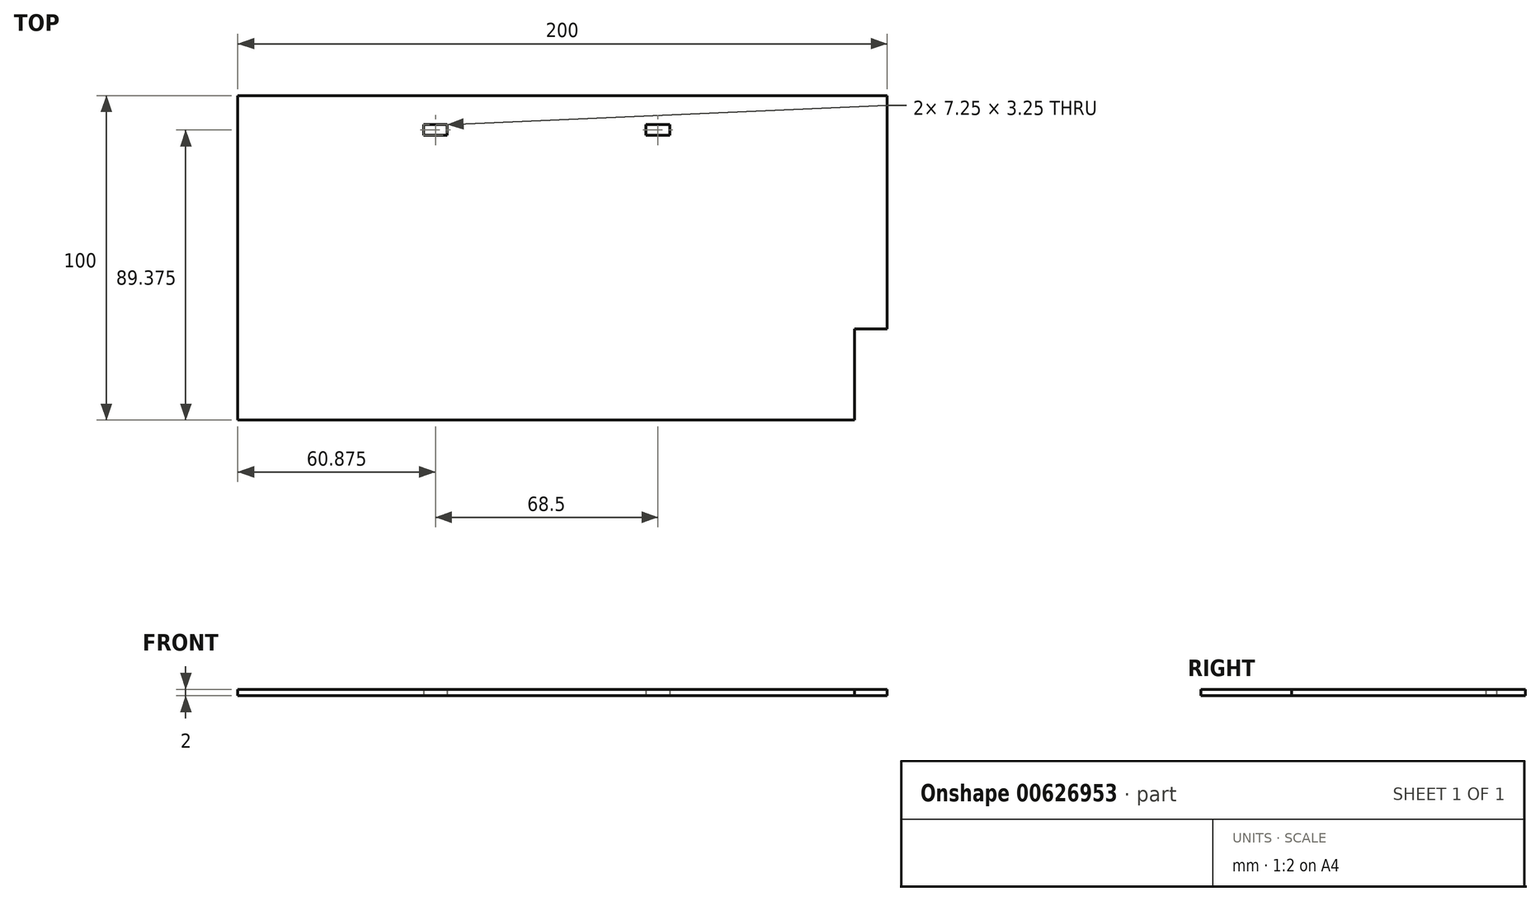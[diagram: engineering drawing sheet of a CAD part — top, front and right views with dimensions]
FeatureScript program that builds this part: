
annotation { "Feature Type Name" : "Feature", "Feature Type Description" : "" }
export const myFeature = defineFeature(function(context is Context, id is Id, definition is map)
    precondition{}
    {
        {
            var Q0;
            Q0=qCreatedBy(makeId("Top.planeOp"),FACE);
            var sketch = newSketch(context, id + "F0", { "sketchPlane" : qUnion([Q0])});
            skLineSegment(sketch, "E0.bottom", {"start": v(100, 50) * mm, "end": v(-100, 50) * mm});
            skLineSegment(sketch, "E0.top", {"start": v(90, -50) * mm, "end": v(-100, -50) * mm});
            skLineSegment(sketch, "E0.left", {"start": v(100, 50) * mm, "end": v(100, -22) * mm});
            skLineSegment(sketch, "E0.right", {"start": v(-100, 50) * mm, "end": v(-100, -50) * mm});
            skPoint(sketch, "E0.middle", {"position": v(0, 0) * mm});
            skLineSegment(sketch, "E1", {"start": v(90, -50) * mm, "end": v(90, -22) * mm});
            skLineSegment(sketch, "E2", {"start": v(90, -22) * mm, "end": v(100, -22) * mm});
            skPoint(sketch, "E3.orphan", {"position": v(100, -50) * mm});
            skLineSegment(sketch, "E4.bottom", {"start": v(33, 37.75) * mm, "end": v(25.75, 37.75) * mm});
            skLineSegment(sketch, "E4.top", {"start": v(33, 41) * mm, "end": v(25.75, 41) * mm});
            skLineSegment(sketch, "E4.left", {"start": v(33, 37.75) * mm, "end": v(33, 41) * mm});
            skLineSegment(sketch, "E4.right", {"start": v(25.75, 37.75) * mm, "end": v(25.75, 41) * mm});
            skPoint(sketch, "E4.middle", {"position": v(29.38, 39.38) * mm});
            skLineSegment(sketch, "E5.bottom", {"start": v(-35.5, 37.75) * mm, "end": v(-42.75, 37.75) * mm});
            skLineSegment(sketch, "E5.top", {"start": v(-35.5, 41) * mm, "end": v(-42.75, 41) * mm});
            skLineSegment(sketch, "E5.left", {"start": v(-35.5, 37.75) * mm, "end": v(-35.5, 41) * mm});
            skLineSegment(sketch, "E5.right", {"start": v(-42.75, 37.75) * mm, "end": v(-42.75, 41) * mm});
            skPoint(sketch, "E5.middle", {"position": v(-39.12, 39.38) * mm});
            skLineSegment(sketch, "E6", {"start": v(83, -50) * mm, "end": v(83, -36) * mm, "construction": true});
            skLineSegment(sketch, "E7", {"start": v(83, -36) * mm, "end": v(73, -36) * mm, "construction": true});
            skLineSegment(sketch, "E8", {"start": v(73, -36) * mm, "end": v(73, -50) * mm, "construction": true});
            skLineSegment(sketch, "E9", {"start": v(65, -50) * mm, "end": v(65, -36) * mm, "construction": true});
            skLineSegment(sketch, "E10", {"start": v(65, -36) * mm, "end": v(55, -36) * mm, "construction": true});
            skLineSegment(sketch, "E11", {"start": v(55, -36) * mm, "end": v(55, -50) * mm, "construction": true});
            skLineSegment(sketch, "E12", {"start": v(6.5, -50) * mm, "end": v(6.5, -36) * mm, "construction": true});
            skLineSegment(sketch, "E13", {"start": v(6.5, -36) * mm, "end": v(-3.5, -36) * mm, "construction": true});
            skLineSegment(sketch, "E14", {"start": v(-3.5, -36) * mm, "end": v(-3.5, -50) * mm, "construction": true});
            skLineSegment(sketch, "E15", {"start": v(-9.5, -50) * mm, "end": v(-9.5, -36) * mm, "construction": true});
            skLineSegment(sketch, "E16", {"start": v(-9.5, -36) * mm, "end": v(-19.5, -36) * mm, "construction": true});
            skLineSegment(sketch, "E17", {"start": v(-19.5, -36) * mm, "end": v(-19.5, -50) * mm, "construction": true});
            skLineSegment(sketch, "E18", {"start": v(72.5, 46) * mm, "end": v(72.5, 14.5) * mm, "construction": true});
            skLineSegment(sketch, "E19", {"start": v(72.5, 14.5) * mm, "end": v(65, 14.5) * mm, "construction": true});
            skLineSegment(sketch, "E20", {"start": v(65, 14.5) * mm, "end": v(65, 46) * mm, "construction": true});
            skLineSegment(sketch, "E21", {"start": v(65, 46) * mm, "end": v(72.5, 46) * mm, "construction": true});
            skPoint(sketch, "E22.orphan", {"position": v(65, 50) * mm});
            skLineSegment(sketch, "E23.bottom", {"start": v(-31, 46) * mm, "end": v(-23.5, 46) * mm, "construction": true});
            skLineSegment(sketch, "E23.top", {"start": v(-31, 14.5) * mm, "end": v(-23.5, 14.5) * mm, "construction": true});
            skLineSegment(sketch, "E23.left", {"start": v(-31, 46) * mm, "end": v(-31, 14.5) * mm, "construction": true});
            skLineSegment(sketch, "E23.right", {"start": v(-23.5, 46) * mm, "end": v(-23.5, 14.5) * mm, "construction": true});
            skLineSegment(sketch, "E24.bottom", {"start": v(-47.5, 46) * mm, "end": v(-55, 46) * mm, "construction": true});
            skLineSegment(sketch, "E24.top", {"start": v(-47.5, 0) * mm, "end": v(-55, 0) * mm, "construction": true});
            skLineSegment(sketch, "E24.left", {"start": v(-47.5, 46) * mm, "end": v(-47.5, 0) * mm, "construction": true});
            skLineSegment(sketch, "E24.right", {"start": v(-55, 46) * mm, "end": v(-55, 0) * mm, "construction": true});
            skSolve(sketch);
        }
        {
            var Q0;
            Q0=makeQuery(id+"F0.imprint","IMPRINT",FACE,{"disambiguationData":[TD([[makeQuery(id+"F0.imprint","IMPRINT",EDGE,{"derivedFrom":sQuery(id+"F0.wireOp",EDGE,"E0.bottom")}),1.0]])]});
            extrude(context, id + "F1", {"entities" : qUnion([Q0]), "depth" : 2 * mm, "offsetDistance" : 25 * mm});
        }
    });
